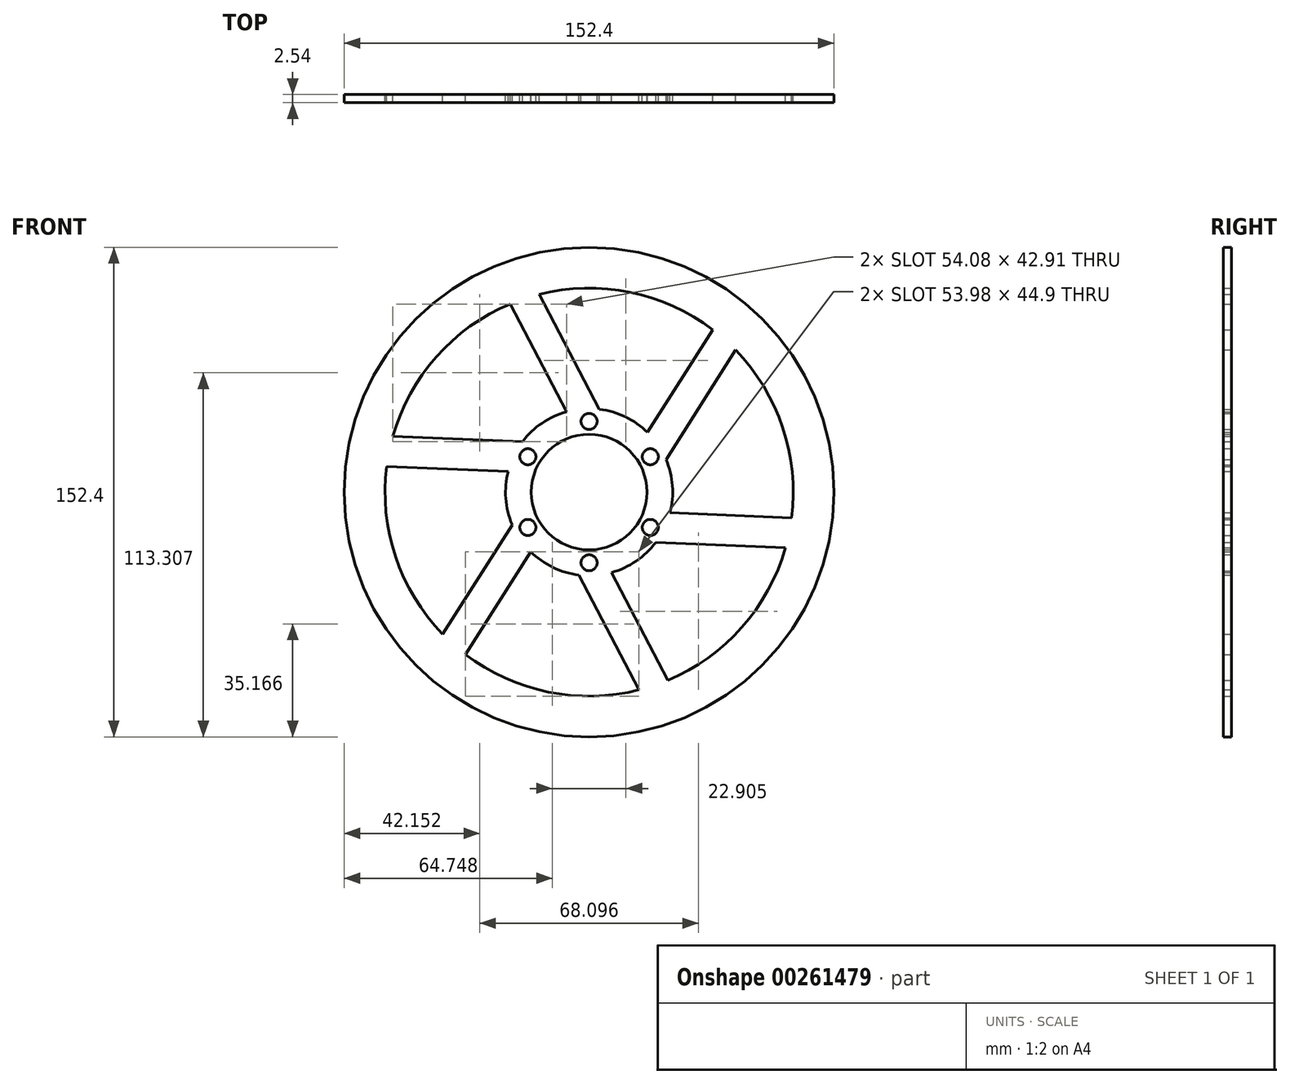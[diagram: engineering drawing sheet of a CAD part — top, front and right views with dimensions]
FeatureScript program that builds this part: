
annotation { "Feature Type Name" : "Feature", "Feature Type Description" : "" }
export const myFeature = defineFeature(function(context is Context, id is Id, definition is map)
    precondition{}
    {
        {
            var Q0;
            Q0=qCreatedBy(makeId("Front.planeOp"),FACE);
            var sketch = newSketch(context, id + "F1", { "sketchPlane" : qUnion([Q0])});
            skCircle(sketch, "E0", {"center": v(0, 0) * mm, "radius": 76.2 * mm});
            skArc(sketch, "E1", {"start": v(-24.55, 58.56) * mm, "mid": v(-47.52, 42.12) * mm, "end": v(-61.09, 17.33) * mm});
            skCircle(sketch, "E2", {"center": v(0, 0) * mm, "radius": 18 * mm});
            skPoint(sketch, "E3", {"position": v(0, 22) * mm});
            skLineSegment(sketch, "E4", {"start": v(15.88, -8.48) * mm, "end": v(15.88, -8.48) * mm});
            skArc(sketch, "E5", {"start": v(-7, 25.04) * mm, "mid": v(-14.65, 21.47) * mm, "end": v(-20.76, 15.65) * mm});
            skLineSegment(sketch, "E6", {"start": v(-7, 25.04) * mm, "end": v(-24.55, 58.56) * mm});
            skLineSegment(sketch, "E7", {"start": v(3.18, 25.8) * mm, "end": v(-15.54, 61.57) * mm});
            skLineSegment(sketch, "E8", {"start": v(0, 0) * mm, "end": v(-46, 0) * mm, "construction": true});
            skLineSegment(sketch, "E9", {"start": v(-46, 0) * mm, "end": v(0, 0) * mm, "construction": true});
            skLineSegment(sketch, "E10", {"start": v(0, 74.48) * mm, "end": v(0, 0) * mm, "construction": true});
            skPoint(sketch, "E11.orphan", {"position": v(-21.56, 73.09) * mm});
            skPoint(sketch, "E12.orphan", {"position": v(-30.45, 69.85) * mm});
            skLineSegment(sketch, "E13.1.0", {"start": v(-25.18, 6.45) * mm, "end": v(-63, 8.02) * mm});
            skLineSegment(sketch, "E13.1.1", {"start": v(-20.76, 15.65) * mm, "end": v(-61.09, 17.33) * mm});
            skLineSegment(sketch, "E13.2.0", {"start": v(-18.18, -18.58) * mm, "end": v(-38.44, -50.54) * mm});
            skLineSegment(sketch, "E13.2.1", {"start": v(-23.93, -10.15) * mm, "end": v(-45.55, -44.24) * mm});
            skLineSegment(sketch, "E14.2.3.0", {"start": v(7, -25.04) * mm, "end": v(24.55, -58.56) * mm});
            skLineSegment(sketch, "E14.3.3.0", {"start": v(-3.18, -25.8) * mm, "end": v(15.54, -61.57) * mm});
            skLineSegment(sketch, "E14.2.4.0", {"start": v(25.18, -6.45) * mm, "end": v(63, -8.02) * mm});
            skLineSegment(sketch, "E14.3.4.0", {"start": v(20.76, -15.65) * mm, "end": v(61.09, -17.33) * mm});
            skLineSegment(sketch, "E14.2.5.0", {"start": v(18.18, 18.58) * mm, "end": v(38.44, 50.54) * mm});
            skLineSegment(sketch, "E14.3.5.0", {"start": v(23.93, 10.15) * mm, "end": v(45.55, 44.24) * mm});
            skPoint(sketch, "E15.1.0", {"position": v(-19.05, 11) * mm});
            skPoint(sketch, "E15.2.0", {"position": v(-19.05, -11) * mm});
            skPoint(sketch, "E15.3.0", {"position": v(0, -22) * mm});
            skPoint(sketch, "E15.4.0", {"position": v(19.05, -11) * mm});
            skPoint(sketch, "E15.5.0", {"position": v(19.05, 11) * mm});
            skArc(sketch, "E16.trimOffspring", {"start": v(-25.18, 6.45) * mm, "mid": v(-25.92, -1.95) * mm, "end": v(-23.93, -10.15) * mm});
            skArc(sketch, "E17.trimOffspring", {"start": v(-18.18, -18.58) * mm, "mid": v(-11.27, -23.43) * mm, "end": v(-3.18, -25.8) * mm});
            skArc(sketch, "E18.trimOffspring", {"start": v(7, -25.04) * mm, "mid": v(14.65, -21.47) * mm, "end": v(20.76, -15.65) * mm});
            skArc(sketch, "E19.trimOffspring", {"start": v(25.18, -6.45) * mm, "mid": v(25.92, 1.95) * mm, "end": v(23.93, 10.15) * mm});
            skArc(sketch, "E20.trimOffspring", {"start": v(18.18, 18.58) * mm, "mid": v(11.27, 23.43) * mm, "end": v(3.18, 25.8) * mm});
            skArc(sketch, "E21.trimOffspring", {"start": v(-38.44, -50.54) * mm, "mid": v(-12.71, -62.21) * mm, "end": v(15.54, -61.57) * mm});
            skArc(sketch, "E22.trimOffspring", {"start": v(24.55, -58.56) * mm, "mid": v(47.52, -42.12) * mm, "end": v(61.09, -17.33) * mm});
            skArc(sketch, "E23.trimOffspring", {"start": v(63, -8.02) * mm, "mid": v(60.24, 20.1) * mm, "end": v(45.55, 44.24) * mm});
            skArc(sketch, "E24.trimOffspring", {"start": v(38.44, 50.54) * mm, "mid": v(12.71, 62.21) * mm, "end": v(-15.54, 61.57) * mm});
            skArc(sketch, "E25.trimOffspring", {"start": v(-63, 8.02) * mm, "mid": v(-60.24, -20.1) * mm, "end": v(-45.55, -44.24) * mm});
            skSolve(sketch);
        }
        {
            var Q0;
            Q0=makeQuery(id+"F1.imprint","IMPRINT",FACE,{"disambiguationData":[TD([[makeQuery(id+"F1.imprint","IMPRINT",EDGE,{"derivedFrom":sQuery(id+"F1.wireOp",EDGE,"E0")}),1.0]])]});
            extrude(context, id + "F2", {"entities" : qUnion([Q0]), "depth" : 2.54 * mm});
        }
        {
            var Q0;
            Q0=sQuery(id+"F1.wireOp",VERTEX,"E15.5.0");
            var Q1;
            Q1=sQuery(id+"F1.wireOp",VERTEX,"E15.4.0");
            var Q2;
            Q2=sQuery(id+"F1.wireOp",VERTEX,"E15.3.0");
            var Q3;
            Q3=sQuery(id+"F1.wireOp",VERTEX,"E15.2.0");
            var Q4;
            Q4=sQuery(id+"F1.wireOp",VERTEX,"E15.1.0");
            var Q5;
            Q5=sQuery(id+"F1.wireOp",VERTEX,"E3");
            var Q6;
            Q6=makeQuery(id+"F2.opExtrude","SWEPT_BODY",BODY,{"disambiguationData":[OSD([sQuery(id+"F1.wireOp",EDGE,"E0"),sQuery(id+"F1.wireOp",EDGE,"E1"),sQuery(id+"F1.wireOp",EDGE,"E2"),sQuery(id+"F1.wireOp",EDGE,"E5"),sQuery(id+"F1.wireOp",EDGE,"E6"),sQuery(id+"F1.wireOp",EDGE,"E7"),sQuery(id+"F1.wireOp",EDGE,"E13.1.0"),sQuery(id+"F1.wireOp",EDGE,"E13.1.1"),sQuery(id+"F1.wireOp",EDGE,"E13.2.0"),sQuery(id+"F1.wireOp",EDGE,"E13.2.1"),sQuery(id+"F1.wireOp",EDGE,"E14.2.3.0"),sQuery(id+"F1.wireOp",EDGE,"E14.3.3.0"),sQuery(id+"F1.wireOp",EDGE,"E14.2.4.0"),sQuery(id+"F1.wireOp",EDGE,"E14.3.4.0"),sQuery(id+"F1.wireOp",EDGE,"E14.2.5.0"),sQuery(id+"F1.wireOp",EDGE,"E14.3.5.0"),sQuery(id+"F1.wireOp",EDGE,"E16.trimOffspring"),sQuery(id+"F1.wireOp",EDGE,"E17.trimOffspring"),sQuery(id+"F1.wireOp",EDGE,"E18.trimOffspring"),sQuery(id+"F1.wireOp",EDGE,"E19.trimOffspring"),sQuery(id+"F1.wireOp",EDGE,"E20.trimOffspring"),sQuery(id+"F1.wireOp",EDGE,"E21.trimOffspring"),sQuery(id+"F1.wireOp",EDGE,"E22.trimOffspring"),sQuery(id+"F1.wireOp",EDGE,"E23.trimOffspring"),sQuery(id+"F1.wireOp",EDGE,"E24.trimOffspring"),sQuery(id+"F1.wireOp",EDGE,"E25.trimOffspring")])]});
            hole(context, id + "F0", {"style" : HoleStyle.SIMPLE, "endStyle" : HoleEndStyle.THROUGH, "oppositeDirection" : true, "holeDiameter" : 5 * mm, "tappedDepth" : 12.7 * mm, "tapClearance" : 3, "locations" : qUnion([Q0, Q1, Q2, Q3, Q4, Q5]), "scope" : qUnion([Q6])});
        }
    });
